FCSTD DOCUMENT  (FreeCAD 1.0R39319 (Git))
Label: top-frame
License: All rights reserved
LicenseURL: http://en.wikipedia.org/wiki/All_rights_reserved
objects: App::Link×7, App::FeaturePython×7, Assembly::JointGroup×1, Assembly::AssemblyObject×1
EXTERNAL_REF file=../parts/steel-profile-40x40x400.FCStd obj=Part

FEATURE [App::Link] steel_profile_40x40x400  label="steel-profile-40x40x400"
  LinkedObject = -> <external ../parts/steel-profile-40x40x400.FCStd>#Part
FEATURE [App::FeaturePython] GroundedJoint  # Assembly grounded joint (typed FeaturePython)
  ObjectToGround = -> steel_profile_40x40x400
FEATURE [App::Link] steel_profile_40x40x401  label="steel-profile-40x40x401"
  LinkPlacement = pos=(440,0,4e-05) rot=(0,0,1;0rad)
  LinkedObject = -> <external ../parts/steel-profile-40x40x400.FCStd>#Part
  Placement = pos=(440,0,4e-05) rot=(0,0,1;0rad)
FEATURE [App::Link] steel_profile_40x40x402  label="steel-profile-40x40x402"
  LinkPlacement = pos=(0,440,0) rot=(0,0,1;0rad)
  LinkedObject = -> <external ../parts/steel-profile-40x40x400.FCStd>#Part
  Placement = pos=(0,440,0) rot=(0,0,1;0rad)
FEATURE [App::Link] steel_profile_40x40x403  label="steel-profile-40x40x403"
  LinkPlacement = pos=(440,440,0) rot=(0,0,1;0rad)
  LinkedObject = -> <external ../parts/steel-profile-40x40x400.FCStd>#Part
  Placement = pos=(440,440,0) rot=(0,0,1;0rad)
FEATURE [App::Link] steel_profile_40x40x404  label="steel-profile-40x40x404"
  LinkPlacement = pos=(40,40,376.43) rot=(0.57735,-0.57735,0.57735;4.18879rad)
  LinkedObject = -> <external ../parts/steel-profile-40x40x400.FCStd>#Part
  Placement = pos=(40,40,376.43) rot=(0.57735,-0.57735,0.57735;4.18879rad)
FEATURE [App::Link] steel_profile_40x40x405  label="steel-profile-40x40x405"
  LinkPlacement = pos=(440,440,360) rot=(0,-1,0;1.5708rad)
  LinkedObject = -> <external ../parts/steel-profile-40x40x400.FCStd>#Part
  Placement = pos=(440,440,360) rot=(0,-1,0;1.5708rad)
FEATURE [App::FeaturePython] GroundedJoint002  # Assembly grounded joint (typed FeaturePython)
  ObjectToGround = -> steel_profile_40x40x401
  Placement = pos=(440,0,4e-05) rot=(0,0,1;0rad)
FEATURE [App::FeaturePython] GroundedJoint006  # Assembly grounded joint (typed FeaturePython)
  ObjectToGround = -> steel_profile_40x40x402
  Placement = pos=(0,440,0) rot=(0,0,1;0rad)
FEATURE [App::FeaturePython] GroundedJoint007  # Assembly grounded joint (typed FeaturePython)
  ObjectToGround = -> steel_profile_40x40x403
  Placement = pos=(440,440,0) rot=(0,0,1;0rad)
FEATURE [App::FeaturePython] GroundedJoint008  # Assembly grounded joint (typed FeaturePython)
  ObjectToGround = -> steel_profile_40x40x405
  Placement = pos=(440,440,360) rot=(0,-1,0;1.5708rad)
FEATURE [App::Link] steel_profile_40x40x406  label="steel-profile-40x40x406"
  LinkPlacement = pos=(3,40,400) rot=(1,0,0;4.71239rad)
  LinkedObject = -> <external ../parts/steel-profile-40x40x400.FCStd>#Part
  Placement = pos=(3,40,400) rot=(1,0,0;4.71239rad)
FEATURE [App::FeaturePython] Joint  label="Parallel"  # Assembly joint (typed FeaturePython)
  Activated = true
  AngleMax = 0
  AngleMin = 0
  Detach1 = false
  Detach2 = false
  Distance = 0
  Distance2 = 0
  EnableAngleMax = false
  EnableAngleMin = false
  EnableLengthMax = false
  EnableLengthMin = false
  JointType = 6 (Parallel)
  LengthMax = 0
  LengthMin = 0
  Placement1 = pos=(40,20,200) rot=(-0.57735,-0.57735,0.57735;2.0944rad)
  Placement2 = pos=(40,20,200) rot=(-0.57735,-0.57735,0.57735;2.0944rad)
  Reference1 = -> Assembly [steel_profile_40x40x406.Body.Face3,steel_profile_40x40x406.Body.Face3]
  Reference2 = -> Assembly [steel_profile_40x40x402.Body.Face3,steel_profile_40x40x402.Body.Face3]
FEATURE [App::FeaturePython] GroundedJoint009  # Assembly grounded joint (typed FeaturePython)
  ObjectToGround = -> steel_profile_40x40x404
  Placement = pos=(40,40,376.43) rot=(0.57735,-0.57735,0.57735;4.18879rad)
FEATURE [Assembly::JointGroup] Joints
  Group = -> [GroundedJoint,GroundedJoint002,GroundedJoint006,GroundedJoint007,GroundedJoint008,Joint,GroundedJoint009]
FEATURE [Assembly::AssemblyObject] Assembly  label="top-frame"
  Group = -> [Joints,steel_profile_40x40x400,GroundedJoint,steel_profile_40x40x401,steel_profile_40x40x402,steel_profile_40x40x403,steel_profile_40x40x404,steel_profile_40x40x405,GroundedJoint002,GroundedJoint006,GroundedJoint007,GroundedJoint008,steel_profile_40x40x406,Joint,GroundedJoint009]
  Origin = -> Origin
  Type = Assembly

RESOLVED EXTERNAL PARTS (link-assembly join: the EXTERNAL_REF files above that resolve inside this repo's crawl, each included once):
---- part ../parts/steel-profile-40x40x400.FCStd = doc fcstd_9b98702d31b4 ----
FCSTD DOCUMENT  (FreeCAD 1.0R39319 (Git))
Label: steel-profile-40x40x400
License: All rights reserved
LicenseURL: http://en.wikipedia.org/wiki/All_rights_reserved
objects: Sketcher::SketchObject×1, PartDesign::Pad×1, PartDesign::Body×1, App::Part×1
note: 6 computed .brp shape members not serialized (recipe doc carries the construction recipe); baked Part::Feature solids carry a one-line shape summary decoded from their .brp

FEATURE [Sketcher::SketchObject] Sketch
  ArcFitTolerance = 1e-06
  AttachmentSupport = -> [XY_Plane001]
  FullyConstrained = true
  MakeInternals = false
  MapMode = 5
  sketch-geometry (18):
    g0: LineSegment StartX=2 StartY=-9e-16 StartZ=0 EndX=38 EndY=-9e-16 EndZ=0
    g1: LineSegment StartX=40 StartY=2 StartZ=0 EndX=40 EndY=38 EndZ=0
    g2: LineSegment StartX=38 StartY=40 StartZ=0 EndX=2 EndY=40 EndZ=0
    g3: LineSegment StartX=-1.3e-15 StartY=38 StartZ=0 EndX=-1.3e-15 EndY=2 EndZ=0
    g4: ArcOfCircle CenterX=2 CenterY=2 CenterZ=0 NormalX=0 NormalY=0 NormalZ=1 AngleXU=0 Radius=2 StartAngle=3.14159 EndAngle=4.71239
    g5: ArcOfCircle CenterX=38 CenterY=2 CenterZ=0 NormalX=0 NormalY=0 NormalZ=1 AngleXU=0 Radius=2 StartAngle=4.71239 EndAngle=6.28319
    g6: ArcOfCircle CenterX=38 CenterY=38 CenterZ=0 NormalX=0 NormalY=0 NormalZ=1 AngleXU=0 Radius=2 StartAngle=0 EndAngle=1.5708
    g7: ArcOfCircle CenterX=2 CenterY=38 CenterZ=0 NormalX=0 NormalY=0 NormalZ=1 AngleXU=0 Radius=2 StartAngle=1.5708 EndAngle=3.14159
    g8: LineSegment StartX=3 StartY=3 StartZ=0 EndX=37 EndY=3 EndZ=0
    g9: LineSegment StartX=37 StartY=3 StartZ=0 EndX=37 EndY=37 EndZ=0
    g10: LineSegment StartX=37 StartY=37 StartZ=0 EndX=3 EndY=37 EndZ=0
    g11: LineSegment StartX=3 StartY=37 StartZ=0 EndX=3 EndY=3 EndZ=0
    g12: LineSegment [constr] StartX=2 StartY=2 StartZ=0 EndX=3 EndY=3 EndZ=0
    g13: LineSegment [constr] StartX=38 StartY=2 StartZ=0 EndX=37 EndY=3 EndZ=0
    g14: LineSegment [constr] StartX=38 StartY=38 StartZ=0 EndX=37 EndY=37 EndZ=0
    g15: LineSegment [constr] StartX=2 StartY=38 StartZ=0 EndX=3 EndY=37 EndZ=0
    g16: GeomPoint [constr] X=-1.6e-15 Y=-1.1e-15 Z=0
    g17: GeomPoint [constr] X=40 Y=40 Z=0
  constraints (43):
    c: Tangent(g0,g4) = -1.5708
    c: Tangent(g0,g5) = -1.5708
    c: Tangent(g1,g5) = -1.5708
    c: Tangent(g1,g6) = -1.5708
    c: Tangent(g2,g6) = -1.5708
    c: Tangent(g2,g7) = -1.5708
    c: Tangent(g3,g7) = -1.5708
    c: Tangent(g3,g4) = -1.5708
    c: Horizontal(g0)
    c: Horizontal(g2)
    c: Vertical(g1)
    c: Vertical(g3)
    c: Equal(g4,g5)
    c: Equal(g5,g6)
    c: Equal(g6,g7)
    c: Coincident(g8,g9)
    c: Coincident(g9,g10)
    c: Coincident(g10,g11)
    c: Coincident(g11,g8)
    c: Horizontal(g8)
    c: Horizontal(g10)
    c: Vertical(g9)
    c: Vertical(g11)
    c: Coincident(g12,g4)
    c: Coincident(g12,g8)
    c: Coincident(g13,g5)
    c: Coincident(g13,g9)
    c: Coincident(g14,g6)
    c: Coincident(g14,g10)
    c: Coincident(g15,g7)
    c: Coincident(g15,g11)
    c: Perpendicular(g12,g13)
    c: Perpendicular(g13,g14)
    c: Perpendicular(g14,g15)
    c: PointOnObject(g16,g0)
    c: PointOnObject(g16,g3)
    c: PointOnObject(g17,g1)
    c: PointOnObject(g17,g2)
    c: Distance(g1,g3) = 40
    c: Distance(g0,g2) = 40
    c: Radius(g5) = 2
    c: Distance(g8,g0) = 3
    c: Coincident(g16,g-1)
FEATURE [PartDesign::Pad] Pad
  Direction = (0,0,1)
  Length = 400
  Length2 = 10
  Profile = -> Sketch
  ReferenceAxis = -> Sketch [N_Axis]
  Suppressed = false
  Type = 0
FEATURE [PartDesign::Body] Body
  AllowCompound = false
  Group = -> [Sketch,Pad]
  Origin = -> Origin001
  Tip = -> Pad
FEATURE [App::Part] Part  label="steel-profile-40x40x400"
  Group = -> [Body]
  Origin = -> Origin
